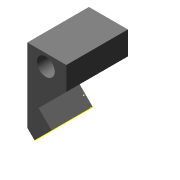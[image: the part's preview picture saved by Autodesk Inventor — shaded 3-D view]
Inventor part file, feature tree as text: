
AUTODESK INVENTOR PART (.ipt)
format: ipt  version: 2013 (Build 170138000, 138)  size: 142,848 bytes
history: native  units: mm
features: sketch x9, extrude x6, hole x1
ambient origin geometry x8: Origin, YZ Plane, XZ Plane, XY Plane, X Axis, Y Axis, Z Axis, Center Point
bodies: Solid1 (feature_tree)
feature tree (16):
  extrude  "Extrusion1"  Depth=20.0mm TaperAngle=0.0deg
  extrude  "Extrusion2"  Depth=3.8mm
  hole  "Hole1"  [1 undecoded]
  extrude  "Extrusion6"  Depth=0.5mm
  extrude  "Extrusion7"  Depth=0.5mm
  extrude  "Extrusion8"  Depth=15.0mm TaperAngle=0.0deg
  extrude  "Extrusion9"  Depth=1.0mm
  sketch  "Sketch12"  dims[d12=1.0mm]
  sketch  "Sketch13"  dims[d36=1.0mm d37=1.0mm]
  sketch  "Sketch1"  dims[d0=10.0mm d1=0.0mm d2=20.0mm d3=0.0mm]
  sketch  "Sketch2"  dims[d4=4.318mm d5=6.0mm d6=8.433mm d7=2.0mm d8=14.3117mm d9=31.0mm d10=20.594885mm d41=3.8mm]
  sketch  "Sketch3"  dims[d42=8.0mm d43=2.5mm d44=0.0mm]
  sketch  "Sketch8"  dims[d45=0.5mm d46=0.5mm]
  sketch  "Sketch9"  dims[d47=0.5mm d48=0.5mm]
  sketch  "Sketch10"  dims[d49=4.0mm d50=0.0mm d51=15.0mm d52=0.0mm]
  sketch  "Sketch11"  dims[d53=0.5mm d54=0.0mm d11=1.0mm]
note: 1 required parameter value undecoded (feature->parameter linkage not recoverable at this tier; creation-order binding heuristic only, values carry confidence <= 0.55)
